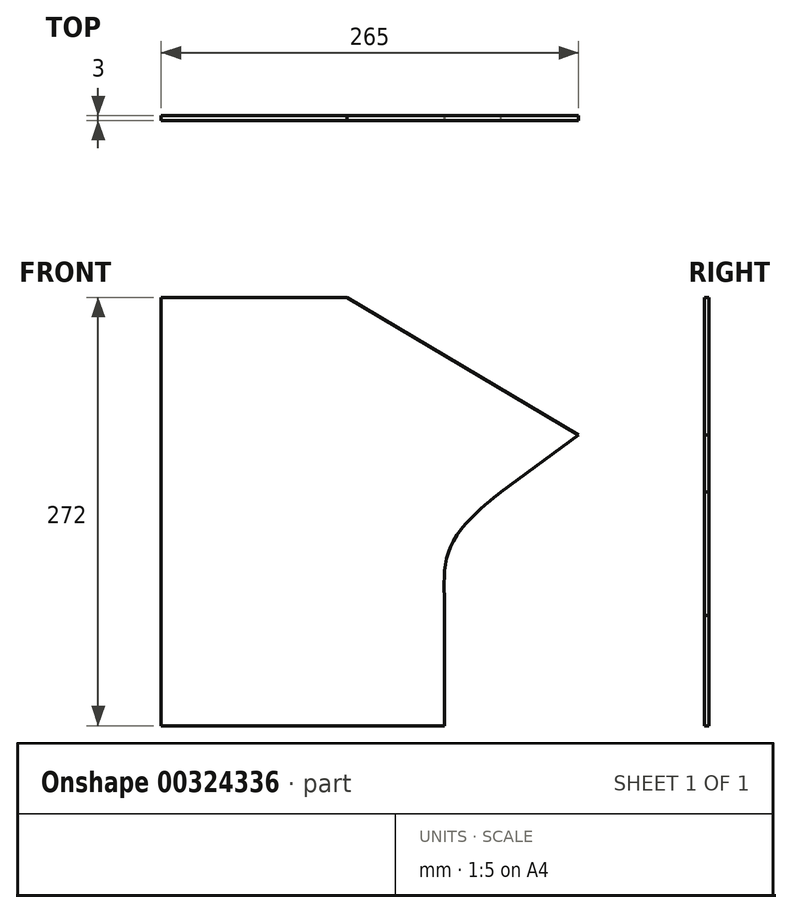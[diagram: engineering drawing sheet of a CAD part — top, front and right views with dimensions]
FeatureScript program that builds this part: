
annotation { "Feature Type Name" : "Feature", "Feature Type Description" : "" }
export const myFeature = defineFeature(function(context is Context, id is Id, definition is map)
    precondition{}
    {
        {
            var Q0;
            Q0=qCreatedBy(makeId("Front.planeOp"),FACE);
            var sketch = newSketch(context, id + "F0", { "sketchPlane" : qUnion([Q0])});
            skLineSegment(sketch, "E0", {"start": v(0, 0) * mm, "end": v(0, 272) * mm});
            skLineSegment(sketch, "E1", {"start": v(0, 272) * mm, "end": v(118, 272) * mm});
            skLineSegment(sketch, "E2", {"start": v(118, 272) * mm, "end": v(265, 184.64) * mm});
            skLineSegment(sketch, "E3", {"start": v(0, 0) * mm, "end": v(180, 0) * mm});
            skLineSegment(sketch, "E4", {"start": v(180, 0) * mm, "end": v(180, 70) * mm});
            skLineSegment(sketch, "E5", {"start": v(265, 184.64) * mm, "end": v(215.82, 148.55) * mm});
            skFitSpline(sketch, "E6", {"points": [v(215.82, 148.55) * mm, v(184.72, 115.79) * mm, v(180, 70) * mm], "startDerivative": vector(-41.66, -31.27) * mm, "endDerivative": vector(-1.26, -98.17) * mm});
            skSolve(sketch);
        }
        {
            var Q0;
            Q0=makeQuery(id+"F0.imprint","IMPRINT",FACE,{"disambiguationData":[TD([[makeQuery(id+"F0.imprint","IMPRINT",EDGE,{"derivedFrom":sQuery(id+"F0.wireOp",EDGE,"E0")}),-1.0]])]});
            extrude(context, id + "F1", {"entities" : qUnion([Q0]), "depth" : 3 * mm});
        }
    });
